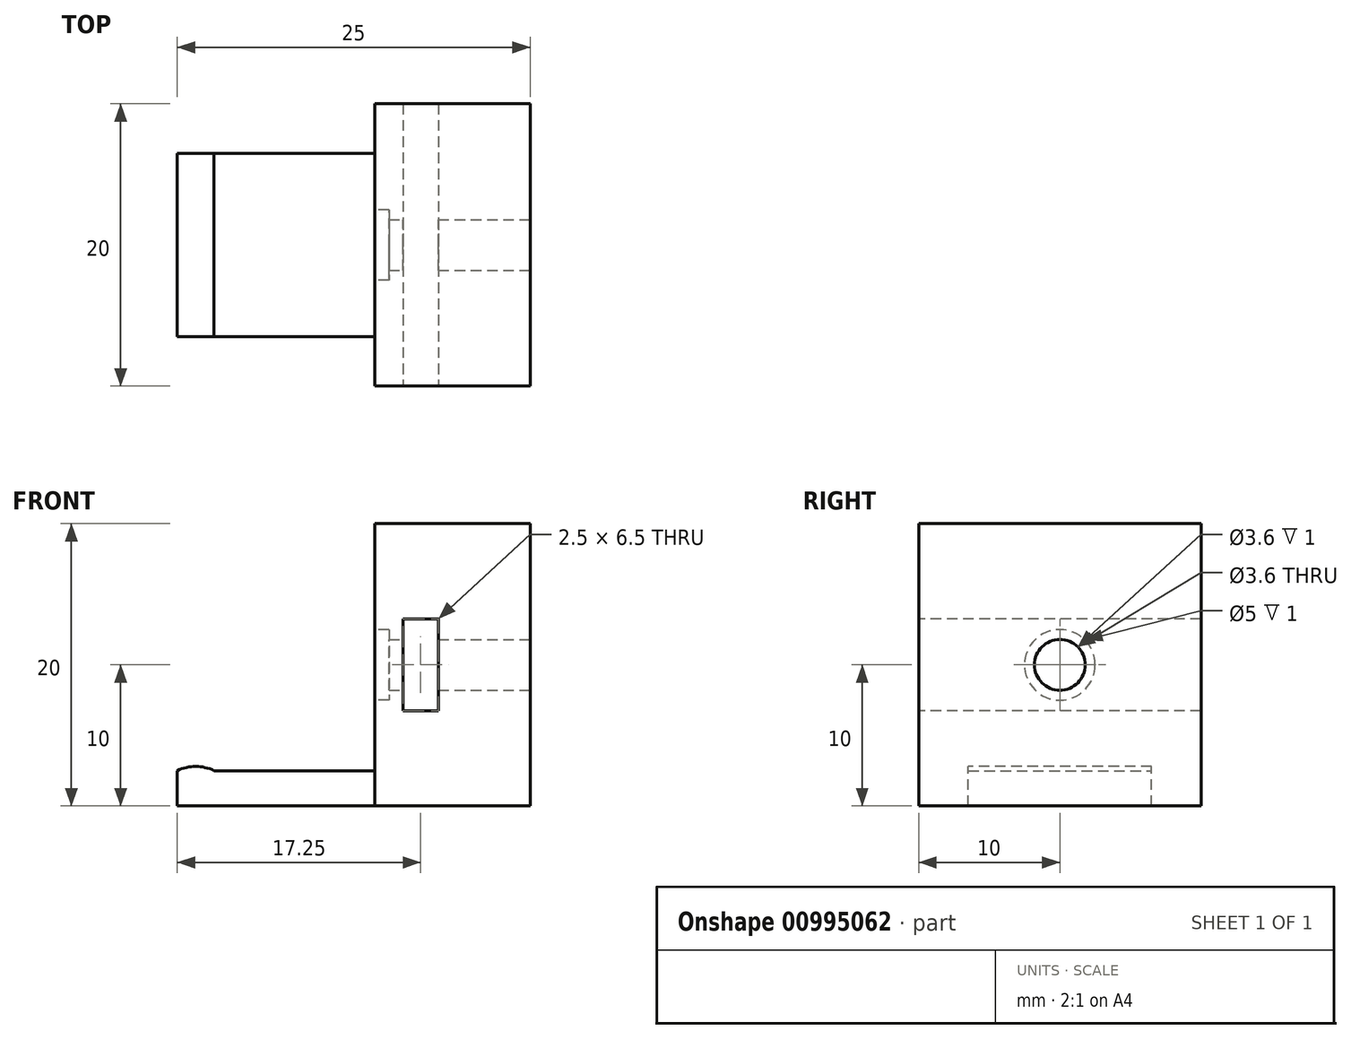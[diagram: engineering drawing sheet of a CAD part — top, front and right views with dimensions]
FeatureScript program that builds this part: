
annotation { "Feature Type Name" : "Feature", "Feature Type Description" : "" }
export const myFeature = defineFeature(function(context is Context, id is Id, definition is map)
    precondition{}
    {
        {
            var Q0;
            Q0=qCreatedBy(makeId("Right.planeOp"),FACE);
            var sketch = newSketch(context, id + "F0", { "sketchPlane" : qUnion([Q0])});
            skLineSegment(sketch, "E0.bottom", {"start": v(10, 10) * mm, "end": v(-10, 10) * mm});
            skLineSegment(sketch, "E0.top", {"start": v(10, -10) * mm, "end": v(-10, -10) * mm});
            skLineSegment(sketch, "E0.left", {"start": v(10, 10) * mm, "end": v(10, -10) * mm});
            skLineSegment(sketch, "E0.right", {"start": v(-10, 10) * mm, "end": v(-10, -10) * mm});
            skPoint(sketch, "E0.middle", {"position": v(0, 0) * mm});
            skCircle(sketch, "E1", {"center": v(0, 0) * mm, "radius": 1.8 * mm});
            skSolve(sketch);
        }
        {
            var Q0;
            Q0=makeQuery(id+"F0.imprint","IMPRINT",FACE,{"disambiguationData":[TD([[makeQuery(id+"F0.imprint","IMPRINT",EDGE,{"derivedFrom":sQuery(id+"F0.wireOp",EDGE,"E0.bottom")}),1.0]])]});
            extrude(context, id + "F1", {"entities" : qUnion([Q0]), "oppositeDirection" : true, "depth" : 11 * mm, "offsetDistance" : 25 * mm});
        }
        {
            var Q0;
            Q0=makeQuery(id+"F1.opExtrude","CAP_FACE",FACE,{"disambiguationData":[OSD([sQuery(id+"F0.wireOp",EDGE,"E0.bottom"),sQuery(id+"F0.wireOp",EDGE,"E0.top"),sQuery(id+"F0.wireOp",EDGE,"E0.left"),sQuery(id+"F0.wireOp",EDGE,"E0.right"),sQuery(id+"F0.wireOp",EDGE,"E1")])],"isStart":false});
            var sketch = newSketch(context, id + "F2", { "sketchPlane" : qUnion([Q0])});
            skLineSegment(sketch, "E2.bottom", {"start": v(6.5, -10) * mm, "end": v(-6.5, -10) * mm});
            skLineSegment(sketch, "E2.top", {"start": v(6.5, -7.5) * mm, "end": v(-6.5, -7.5) * mm});
            skLineSegment(sketch, "E2.left", {"start": v(6.5, -10) * mm, "end": v(6.5, -7.5) * mm});
            skLineSegment(sketch, "E2.right", {"start": v(-6.5, -10) * mm, "end": v(-6.5, -7.5) * mm});
            skLineSegment(sketch, "E3.bottom", {"start": v(-10, -6.5) * mm, "end": v(-7.5, -6.5) * mm});
            skLineSegment(sketch, "E3.top", {"start": v(-10, 6.5) * mm, "end": v(-7.5, 6.5) * mm});
            skLineSegment(sketch, "E3.left", {"start": v(-10, -6.5) * mm, "end": v(-10, 6.5) * mm});
            skLineSegment(sketch, "E3.right", {"start": v(-7.5, -6.5) * mm, "end": v(-7.5, 6.5) * mm});
            skLineSegment(sketch, "E4.bottom", {"start": v(-6.5, 10) * mm, "end": v(6.5, 10) * mm});
            skLineSegment(sketch, "E4.top", {"start": v(-6.5, 7.5) * mm, "end": v(6.5, 7.5) * mm});
            skLineSegment(sketch, "E4.left", {"start": v(-6.5, 10) * mm, "end": v(-6.5, 7.5) * mm});
            skLineSegment(sketch, "E4.right", {"start": v(6.5, 10) * mm, "end": v(6.5, 7.5) * mm});
            skLineSegment(sketch, "E5.bottom", {"start": v(10, 6.5) * mm, "end": v(7.5, 6.5) * mm});
            skLineSegment(sketch, "E5.top", {"start": v(10, -6.5) * mm, "end": v(7.5, -6.5) * mm});
            skLineSegment(sketch, "E5.left", {"start": v(10, 6.5) * mm, "end": v(10, -6.5) * mm});
            skLineSegment(sketch, "E5.right", {"start": v(7.5, 6.5) * mm, "end": v(7.5, -6.5) * mm});
            skLineSegment(sketch, "E6", {"start": v(-7.5, 0) * mm, "end": v(0, 0) * mm, "construction": true});
            skLineSegment(sketch, "E7", {"start": v(0, 0) * mm, "end": v(7.5, 0) * mm, "construction": true});
            skLineSegment(sketch, "E8", {"start": v(0, 7.5) * mm, "end": v(0, 0) * mm, "construction": true});
            skLineSegment(sketch, "E9", {"start": v(0, -7.5) * mm, "end": v(0, 0) * mm, "construction": true});
            skPoint(sketch, "E10", {"position": v(-7.5, 0) * mm});
            skCircle(sketch, "E11", {"center": v(0, 0) * mm, "radius": 2.5 * mm});
            skSolve(sketch);
        }
        {
            var Q0;
            Q0=makeQuery(id+"F2.imprint","IMPRINT",FACE,{"disambiguationData":[TD([[makeQuery(id+"F2.imprint","IMPRINT",EDGE,{"derivedFrom":sQuery(id+"F2.wireOp",EDGE,"E2.bottom")}),1.0]])]});
            extrude(context, id + "F3", {"entities" : qUnion([Q0]), "operationType" : NewBodyOperationType.ADD, "depth" : 14 * mm, "offsetDistance" : 25 * mm});
        }
        {
            var Q0;
            Q0=makeQuery(id+"F2.imprint","IMPRINT",FACE,{"disambiguationData":[TD([[makeQuery(id+"F2.imprint","IMPRINT",EDGE,{"derivedFrom":sQuery(id+"F2.wireOp",EDGE,"E11")}),1.0]])]});
            extrude(context, id + "F4", {"entities" : qUnion([Q0]), "operationType" : NewBodyOperationType.REMOVE, "oppositeDirection" : true, "depth" : 1 * mm, "offsetDistance" : 25 * mm});
        }
        {
            var Q0;
            Q0=makeQuery(id+"F1.opExtrude","SWEPT_FACE",FACE,{"disambiguationData":[OSD([sQuery(id+"F0.wireOp",EDGE,"E0.right")])]});
            var sketch = newSketch(context, id + "F5", { "sketchPlane" : qUnion([Q0])});
            skLineSegment(sketch, "E12.bottom", {"start": v(-6.5, -3.25) * mm, "end": v(-9, -3.25) * mm});
            skLineSegment(sketch, "E12.top", {"start": v(-6.5, 3.25) * mm, "end": v(-9, 3.25) * mm});
            skLineSegment(sketch, "E12.left", {"start": v(-6.5, -3.25) * mm, "end": v(-6.5, 3.25) * mm});
            skLineSegment(sketch, "E12.right", {"start": v(-9, -3.25) * mm, "end": v(-9, 3.25) * mm});
            skPoint(sketch, "E12.middle", {"position": v(-7.75, 0) * mm});
            skSolve(sketch);
        }
        {
            var Q0;
            Q0=makeQuery(id+"F5.imprint","IMPRINT",FACE,{"disambiguationData":[TD([[makeQuery(id+"F5.imprint","IMPRINT",EDGE,{"derivedFrom":sQuery(id+"F5.wireOp",EDGE,"E12.bottom")}),-1.0]])]});
            extrude(context, id + "F6", {"entities" : qUnion([Q0]), "operationType" : NewBodyOperationType.REMOVE, "oppositeDirection" : true, "depth" : 25 * mm, "offsetDistance" : 25 * mm});
        }
        {
            var Q0;
            Q0=makeQuery(id+"F3.opExtrude","SWEPT_FACE",FACE,{"disambiguationData":[OSD([sQuery(id+"F2.wireOp",EDGE,"E2.left")])]});
            var sketch = newSketch(context, id + "F7", { "sketchPlane" : qUnion([Q0])});
            skArc(sketch, "E13", {"start": v(-22.38, -7.5) * mm, "mid": v(-23.7, -7.2) * mm, "end": v(-25, -7.5) * mm});
            skLineSegment(sketch, "E14.0", {"start": v(-25, -7.5) * mm, "end": v(-22.38, -7.5) * mm});
            skPoint(sketch, "E15.orphan", {"position": v(-25, -7.5) * mm});
            skPoint(sketch, "E16.orphan", {"position": v(-11, -7.5) * mm});
            skSolve(sketch);
        }
        {
            var Q0;
            Q0=makeQuery(id+"F7.imprint","IMPRINT",FACE,{"disambiguationData":[TD([[makeQuery(id+"F7.imprint","IMPRINT",EDGE,{"derivedFrom":sQuery(id+"F7.wireOp",EDGE,"E13")}),1.0]])]});
            var Q1;
            Q1=makeQuery(id+"F3.opExtrude","SWEPT_FACE",FACE,{"disambiguationData":[OSD([sQuery(id+"F2.wireOp",EDGE,"E2.right")])]});
            extrude(context, id + "F8", {"entities" : qUnion([Q0]), "operationType" : NewBodyOperationType.ADD, "endBound" : BoundingType.UP_TO_SURFACE, "oppositeDirection" : true, "depth" : 25 * mm, "endBoundEntityFace" : qUnion([Q1]), "offsetDistance" : 25 * mm});
        }
    });
